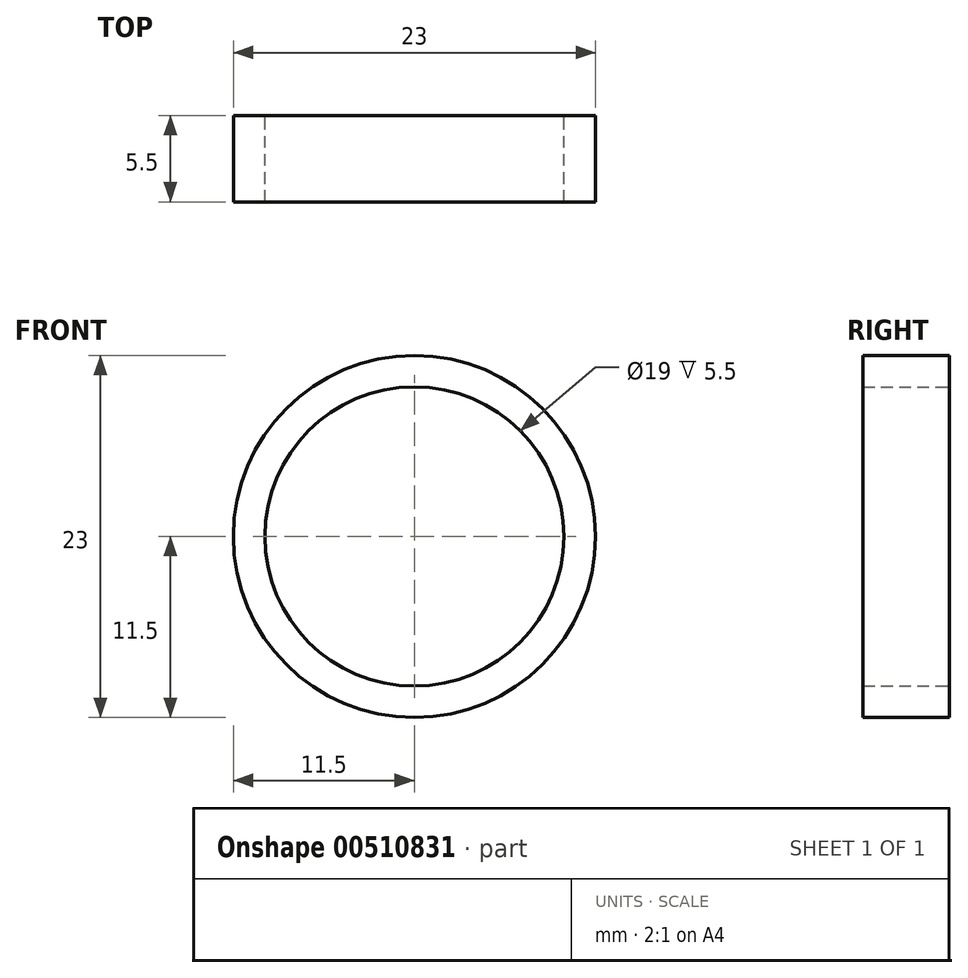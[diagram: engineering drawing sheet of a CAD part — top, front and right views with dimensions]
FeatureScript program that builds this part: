
annotation { "Feature Type Name" : "Feature", "Feature Type Description" : "" }
export const myFeature = defineFeature(function(context is Context, id is Id, definition is map)
    precondition{}
    {
        {
            var Q0;
            Q0=qCreatedBy(makeId("Front.planeOp"),FACE);
            var sketch = newSketch(context, id + "F0", { "sketchPlane" : qUnion([Q0])});
            skCircle(sketch, "E0", {"center": v(0, 0) * mm, "radius": 11.5 * mm});
            skSolve(sketch);
        }
        {
            var Q0;
            Q0 = qSketchRegion(id + "F0", true);
            extrude(context, id + "F1", {"entities" : qUnion([Q0]), "depth" : 5.5 * mm, "offsetDistance" : 25 * mm});
        }
        {
            var Q0;
            Q0=makeQuery(id+"F1.opExtrude","CAP_FACE",FACE,{"disambiguationData":[OSD([sQuery(id+"F0.wireOp",EDGE,"E0")])],"isStart":false});
            var Q1;
            Q1=makeQuery(id+"F1.opExtrude","CAP_FACE",FACE,{"disambiguationData":[OSD([sQuery(id+"F0.wireOp",EDGE,"E0")])],"isStart":true});
            shell(context, id + "F2", {"entities" : qUnion([Q0, Q1]), "thickness" : 2 * mm});
        }
    });
